# Revit family: PLASTIC SAND TRAP BASE DN100 Slot Drain
name_source: partatom
category: Оборудование
units: mm (PartAtom-declared; Revit-internal decimal feet)

## family parameters
Общий = Да
Основа = Грань
При загрузке вырезать с полостями = Нет
Размер круглого соединителя = Использовать диаметр
Тип детали = Нормальный
Точка расчета площади = Нет

## types (2) — shared parameters
A01 = L-type H100 A15-C250 : 20175-1L-100 Galvanized Steel
A02 = L-type H100 A15-C250 : 20975-1L-100 Stainless steel
A03 = T-type H100 A15-C250 : 20175-1T-100 Galvanized Steel
A04 = T-type H100 A15-C250 : 20975-1T-100 Stainless steel
A05 = T-type H25 A15 : 20175-1T-25 Galvanized Steel
A06 = T-type H25 A15 : 20975-1T-25 Stainless steel
A07 = T-type H25 shifted A15 : 20175-1T-25-40 Galvanized Steel
A08 = T-type H25 shifted A15 : 20975-1T-25-40 Stainless steel
A09 = T-type H60-100 A15-C250 : 20975-1T-60-100 Stainless steel
A10 = L-type H25 A15 : 209875-L-25 Plastic
A11 = L-type H100 A15 : 209875-L-100 Plastic
A12 = L-type H100 A15 : 209975-L-100 Stainless steel
ADSK_Dimension_Diameter = 100 мм
ADSK_Dimension_Lenght = 500 мм
ADSK_Dimension_Width = 156 мм
ADSK_Load class = C250
ADSK_Manufacturer = Vodaland
ADSK_Material_Name = Plastic
ADSK_Sealant = 11
ADSK_Unit = pcs
ADSK_Weight = 2.6
Channel = Plastic sand trap Base DN100 : 8080
ConnectorBack = TC : Back
ConnectorFront = TC : Front
ConnectorLeft = TC : Left
ConnectorRight = TC : Right
Dp110 = Dp : 110
Dp160 = Dp : 160
Dp50 = Dp : 50
G01 = Slot Drain Revision L-type H100 Base DN100 Channel A15-C250 : 20175-1L-100
G02 = Slot Drain Revision L-type H100 Base DN100 Channel A15-C250 : 20975-1L-100
G03 = Slot Drain Revision T-type H100 Base DN100 Channel A15-C250 : 20175-1T-100
G04 = Slot Drain Revision T-type H100 Base DN100 Channel A15-C250 : 20975-1T-100
G05 = Slot Drain Revision T-type H25 Base DN100 Channel A15 : 20175-1T-25
G06 = Slot Drain Revision T-type H25 Base DN100 Channel A15 : 20975-1T-25
G07 = Slot Drain Revision T-type H25 for Base DN100 Channel A15 : 20175-1T-25-40
G08 = Slot Drain Revision T-type H25 for Base DN100 Channel A15 : 20975-1T-25-40
G09 = Slot Drain Revision T-type H60-100 for Base DN100 Channel A15-C250 : 20975-1T-60-100
G10 = Slot drain Revision L-type H25 for channel Base DN100 plastic A15 : 209875-L-25
G11 = Slot drain Revision L-type H100 for channel Base DN100 plastic A15 : 209875-L-100
G12 = Slot drain Revision L-type H100 for channel Base DN100 plastic A15 : 209975-L-100
V1G = Да
W1 = 160 мм
W2 = 156 мм
no = No
Группа модели = Linear drainage
zero-valued in all types: Отметка по умолчанию

## per-type parameters (varying)
| type | ADSK_Dimension_Height | ADSK_Name |
| 8080 | 400 мм | Plastic sand trap Base DN100 H500 |
| 8087 | 350 мм | Plastic sand trap Base DN100 H350 reinforced |

note: column(s) folded — value = type name in every type: ADSK_Product code

## geometry (parser evidence)
native form markers: Blend x4
no freeform markers — native parametric forms only
